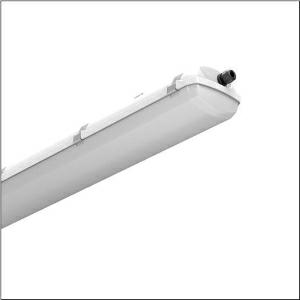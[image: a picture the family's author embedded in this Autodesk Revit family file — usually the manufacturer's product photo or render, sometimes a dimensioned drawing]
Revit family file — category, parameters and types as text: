
# Revit family: monsun_ex_51fxb1dp670a
name_source: partatom
category: Lighting Fixtures
units: mm (PartAtom-declared; Revit-internal decimal feet)

## family parameters
Cut with Voids When Loaded = No
Host = Face
Light Source = No
Part Type = Normal
Room Calculation Point = No
Round Connector Dimension = Use Diameter
Shared = No

## types (1)
- Monsun Ex (1 x LED, 7310 lm, 43.8 W, 6500K)
    Apparent Load = 44 VA
    CIE Flux Codes = 61 86 97 100 100
    Color Rendering = 80
    Color Temperature = 6500K
    Default Elevation = 1800 mm
    Description = Monsun Ex, damp-proof luminaire, primary optical cover: cover, of PC, UV-stabilised, opal, light emission: direct distribution, primary light characteristic: symmetric, installation type: surface-mounted, LED, rated luminous flux: 7.310lm, luminous efficacy: 167lm/W, light colour: 865, colour temperature: 6500K, control gear: DALI 2, with terminal, 5-pole, max. 2.5mm², through-wiring: 7x 2.5mm², mains connection: 220..240V, AC, 50/60Hz, rated input power: 44W, housing, of PC, light grey (RAL 7035), incl. blanking plug, incl. 2x Ex cable gland M20 for cable diameter 7..12mm with sealing, length: 1.580mm, width: 155mm, height: 105mm, clip for enclosure, of stainless steel, protection rating (complete): IP66, insulation class (complete): insulation class I (protective earthing), certification: CE, explosion class: zone2,22 II 3G Ex nR IIC T6 GC, II 3D Ex tc IIIC T80°C Dc, impact resistance: IK10, permissible operating ambient temperature: -20..+60°C, LABS conformity tested according to VDMA 24364:2018-05, contact your sales advisor before using the luminaires in applications with unclear chemical exposure, large temperature fluctuations or condensation-forming humidity, packaging unit: 1 piece
    Height = 105 mm
    Lamp = 1 x LED
    Lamp Light Flux = 7310 lm
    Lamp Power = 43.8 W
    Lamp count = 1
    Length = 1580 mm
    Luminous efficacy = 167 lm/W
    Manufacturer = Siteco
    ModVariant = No
    Model = 51FXB1DP670A
    Mounting Place = Ceiling
    Mounting Type = Surface mounted
    Number of Poles = 1
    OnlyDefault = Yes
    Power Factor = 1
    Product Name = Monsun Ex
    Product group = damp-proof luminaire
    ProductGroupID = 300
    Protection Class = Protection class I
    Protection Degree = IP 66
    RLX_Detail_Level = 1
    RLX_Emergency_Light_Flux = 0 lm
    RLX_Emergency_Type = 0
    RLX_Emergency_Type_DB = No
    RlxData = <blob elided: 41785 chars, md5=fe6de2d4>
    Socket = socket
    Standby Power = 0 W
    System Light Flux = 7310 lm
    System Power = 44 W
    Type Comments = Product without accessories
    Type Image = l_1258882.jpg
    URL = http://relux.com
    VarID = ---
    Voltage = 0 V
    Weight = 0.00 kg
    Width = 155 mm

## geometry (parser evidence)
native form markers: Blend x4, Sweep x12
no freeform markers — native parametric forms only
